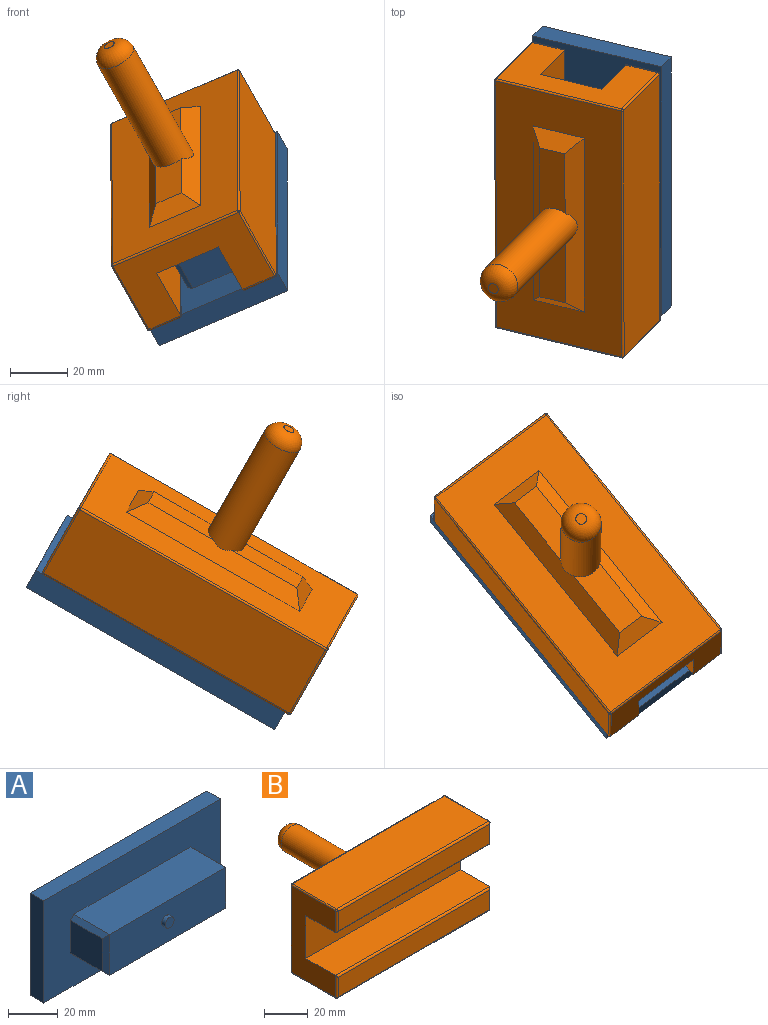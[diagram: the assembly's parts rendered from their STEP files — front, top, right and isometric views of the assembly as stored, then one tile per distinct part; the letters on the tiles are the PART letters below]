
ASSEMBLY  parts=2 mates=1
PART A: 19 faces, bbox 100x29.8x50 mm
  f0: plane 50x7.8mm, normal (-1,0,0), area 389.9mm2, adj f1,f3,f4,f5
  f1: plane 100x7.8mm, normal (0,0,-1), area 779.8mm2, adj f0,f2,f4,f5
  f2: plane 50x7.8mm, normal (1,0,0), area 389.9mm2, adj f1,f3,f4,f5
  f3: plane 100x7.8mm, normal (0,0,1), area 779.8mm2, adj f0,f2,f4,f5
  f4: plane 100x50mm, normal (0,-1,0), area 3608mm2, adj f0,f1,f2,f3,f6,f7,f8,f9
  f5: plane 100x50mm, normal (0,1,0), area 5000mm2, adj f0,f1,f2,f3
  f6: plane 18x16mm, normal (-1,0,0), area 288mm2, adj f4,f14,f15,f16
  f7: plane 66x20mm, normal (0,0,-1), area 1320mm2, adj f4,f10,f12,f15
  f8: plane 18x16mm, normal (1,0,0), area 288mm2, adj f4,f11,f12,f13
  f9: plane 66x20mm, normal (0,0,1), area 1320mm2, adj f4,f10,f11,f14
  f10: plane 66x20mm, normal (0,-1,0), area 1300.4mm2, adj f7,f9,f13,f16,f17
  f11: plane 20x2mm, normal (0.71,0,0.71), area 53.7mm2, adj f4,f8,f9,f13
  f12: plane 20x2mm, normal (0.71,0,-0.71), area 53.7mm2, adj f4,f7,f8,f13
  f13: plane 20x2mm, normal (0.71,-0.71,0), area 50.9mm2, adj f8,f10,f11,f12
  f14: plane 20x2mm, normal (-0.71,0,0.71), area 53.7mm2, adj f4,f6,f9,f16
  f15: plane 20x2mm, normal (-0.71,0,-0.71), area 53.7mm2, adj f4,f6,f7,f16
  f16: plane 20x2mm, normal (-0.71,-0.71,0), area 50.9mm2, adj f6,f10,f14,f15
  f17: cylinder r=2.5mm len=5mm, axis (0,1,0), area 31.4mm2, adj f10,f18
  f18: plane 5x5mm, normal (0,-1,0), area 19.6mm2, adj f17
PART B: 43 faces, bbox 100x84.1x50 mm
  f0: plane 26.38x9.84mm, normal (0,1,0), area 233mm2, adj f12,f14,f15,f16
  f1: plane 98.75x48.75mm, normal (0,1,0), area 3428.8mm2, adj f14,f15,f16,f17,f32,f33,f37,f38
  f2: plane 100x24mm, normal (0,-1,0), area 2400mm2, adj f3,f5,f7,f9
  f3: plane 48.75x28.38mm, normal (-1,0,0), area 927.4mm2, adj f2,f7,f9,f19,f22,f27,f31,f32
  f4: plane 98.75x28.38mm, normal (0,0,-1), area 2802.2mm2, adj f21,f27,f33,f34
  f5: plane 48.75x28.38mm, normal (1,0,0), area 927.4mm2, adj f2,f7,f9,f20,f25,f34,f38,f40
  f6: plane 98.75x28.38mm, normal (0,0,1), area 2802.2mm2, adj f24,f31,f37,f40
  f7: plane 100x19mm, normal (0,0,-1), area 1900mm2, adj f2,f3,f5,f23
  f8: plane 98x11mm, normal (0,-1,0), area 1078mm2, adj f22,f23,f24,f25
  f9: plane 100x19mm, normal (0,0,1), area 1900mm2, adj f2,f3,f5,f18
  f10: plane 98x11mm, normal (0,-1,0), area 1078mm2, adj f18,f19,f20,f21
  f11: plane 26.37x9.84mm, normal (0,1,0), area 233mm2, adj f12,f15,f16,f17
  f12: cylinder r=7mm len=47.2mm, axis (0,-1,0), area 1969.1mm2, adj f0,f11,f15,f16,f42
  f13: plane 3.84x3.84mm, normal (0,1,0), area 11.6mm2, adj f42
  f14: plane 19.84x5mm, normal (0.71,0.71,0), area 104.9mm2, adj f0,f1,f15,f16
  f15: plane 69.84x5mm, normal (0,0.71,0.71), area 421.1mm2, adj f0,f1,f11,f12,f14,f17
  f16: plane 69.84x5mm, normal (0,0.71,-0.71), area 451.9mm2, adj f0,f1,f11,f12,f14,f17
  f17: plane 19.84x5mm, normal (-0.71,0.71,0), area 104.9mm2, adj f1,f11,f15,f16
  f18: cylinder r=1mm len=100mm, axis (1,0,0), area 155.9mm2, adj f9,f10,f19,f20
  f19: cylinder r=1mm len=12.38mm, axis (0,0,1), area 18.7mm2, adj f3,f10,f18,f26
  f20: cylinder r=1mm len=12.38mm, axis (0,0,-1), area 18.7mm2, adj f5,f10,f18,f30
  f21: cylinder r=1mm len=98.75mm, axis (-1,0,0), area 154.7mm2, adj f4,f10,f26,f30
  f22: cylinder r=1mm len=12.38mm, axis (0,0,1), area 18.7mm2, adj f3,f8,f23,f28
  f23: cylinder r=1mm len=100mm, axis (-1,0,0), area 155.9mm2, adj f7,f8,f22,f25
  f24: cylinder r=1mm len=98.75mm, axis (1,0,0), area 154.7mm2, adj f6,f8,f28,f41
  f25: cylinder r=1mm len=12.38mm, axis (0,0,-1), area 18.7mm2, adj f5,f8,f23,f41
  f26: bspline ~1.21x1mm, area 1mm2, adj f19,f21,f27
  f27: cylinder r=0.62mm len=28.38mm, axis (0,-1,0), area 27.8mm2, adj f3,f4,f26,f29
  f28: bspline ~1.21x1mm, area 1mm2, adj f22,f24,f31
  f29: sphere r=0.62mm, area 0.6mm2, adj f27,f32,f33
  f30: bspline ~1.21x1mm, area 1mm2, adj f20,f21,f34
  f31: cylinder r=0.62mm len=28.38mm, axis (0,1,0), area 27.8mm2, adj f3,f6,f28,f35
  f32: cylinder r=0.62mm len=48.75mm, axis (0,0,-1), area 47.8mm2, adj f1,f3,f29,f35
  f33: cylinder r=0.62mm len=98.75mm, axis (1,0,0), area 96.7mm2, adj f1,f4,f29,f36
  f34: cylinder r=0.62mm len=28.38mm, axis (0,1,0), area 27.8mm2, adj f4,f5,f30,f36
  f35: sphere r=0.62mm, area 0.6mm2, adj f31,f32,f37
  f36: sphere r=0.62mm, area 0.6mm2, adj f33,f34,f38
  f37: cylinder r=0.62mm len=98.75mm, axis (-1,0,0), area 96.7mm2, adj f1,f6,f35,f39
  f38: cylinder r=0.62mm len=48.75mm, axis (0,0,1), area 47.8mm2, adj f1,f5,f36,f39
  f39: sphere r=0.62mm, area 0.6mm2, adj f37,f38,f40
  f40: cylinder r=0.62mm len=28.38mm, axis (0,-1,0), area 27.8mm2, adj f5,f6,f39,f41
  f41: bspline ~1.21x1mm, area 1mm2, adj f24,f25,f40
  f42: torus R=1.92mm, axis (0,1,0), area 258.4mm2, adj f12,f13
PLACE A rot(axis=(-0.56,-0.79,0.24),118deg) t=(-42.36,-128.15,88.36)mm
PLACE B rot(axis=(0.59,0.24,0.77),122.2deg) t=(-104.14,-135.88,97.24)mm
MATE parallel A.f10 <-> B.f2  axis (-0.44,-0.45,0.78) through (-77.14,-91.69,125.23)mm
